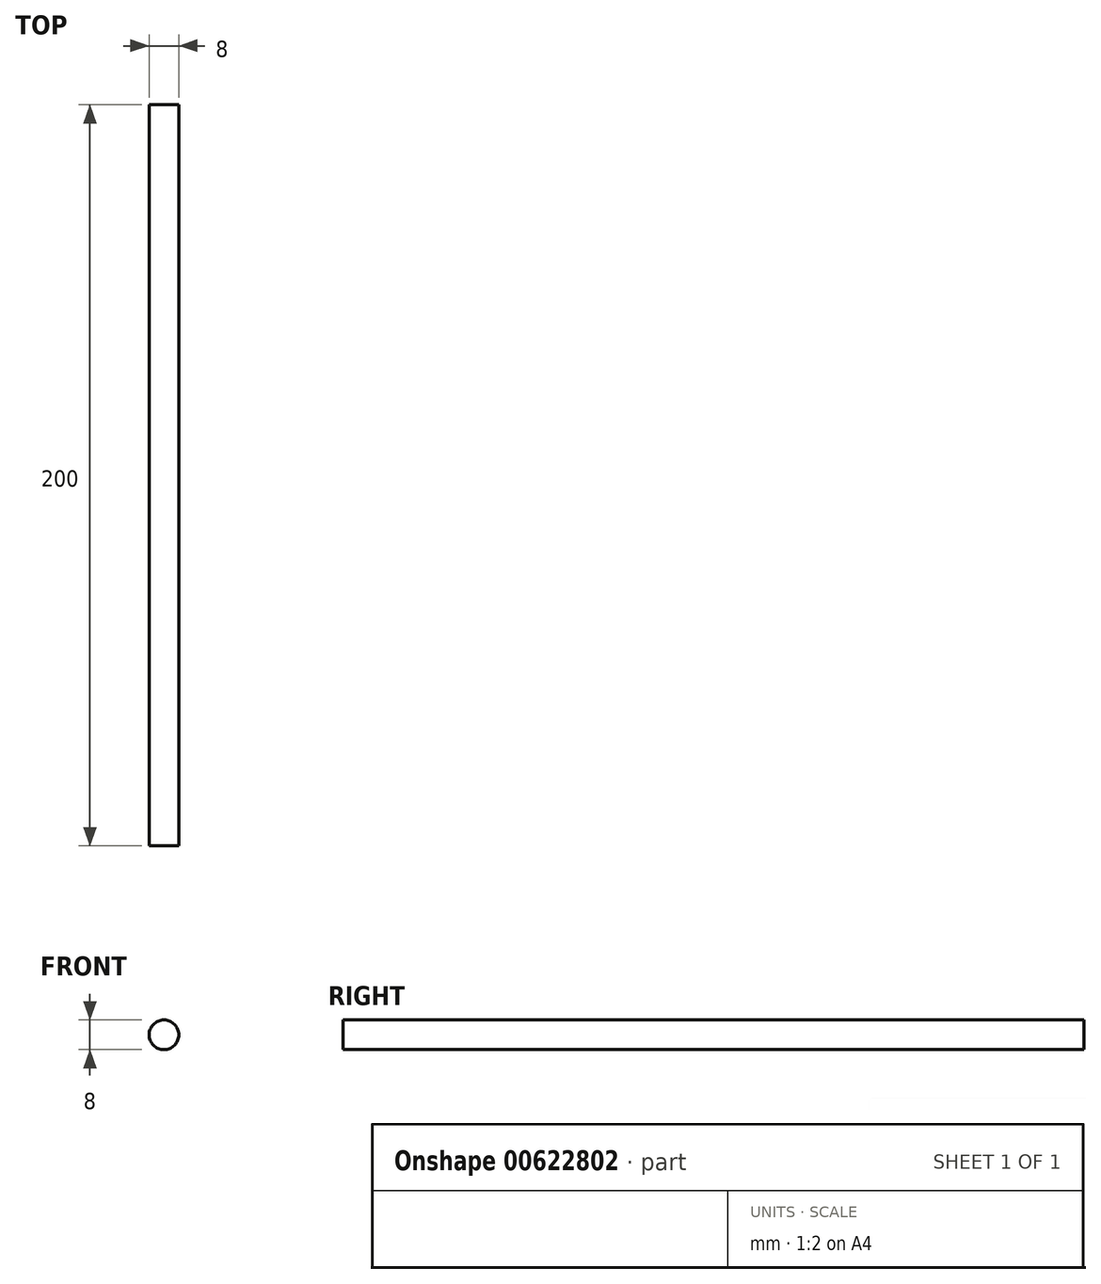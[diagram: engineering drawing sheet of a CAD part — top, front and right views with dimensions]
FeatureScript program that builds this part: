
annotation { "Feature Type Name" : "Feature", "Feature Type Description" : "" }
export const myFeature = defineFeature(function(context is Context, id is Id, definition is map)
    precondition{}
    {
        {
            var Q0;
            Q0=qCreatedBy(makeId("Front.planeOp"),FACE);
            var sketch = newSketch(context, id + "F0", { "sketchPlane" : qUnion([Q0])});
            skCircle(sketch, "E0", {"center": v(0, 0) * mm, "radius": 4 * mm});
            skSolve(sketch);
        }
        {
            var Q0;
            Q0=makeQuery(id+"F0.imprint","IMPRINT",FACE,{"disambiguationData":[TD([[makeQuery(id+"F0.imprint","IMPRINT",EDGE,{"derivedFrom":sQuery(id+"F0.wireOp",EDGE,"E0")}),1.0]])]});
            extrude(context, id + "F1", {"entities" : qUnion([Q0]), "depth" : 200 * mm, "offsetDistance" : 25 * mm});
        }
    });
